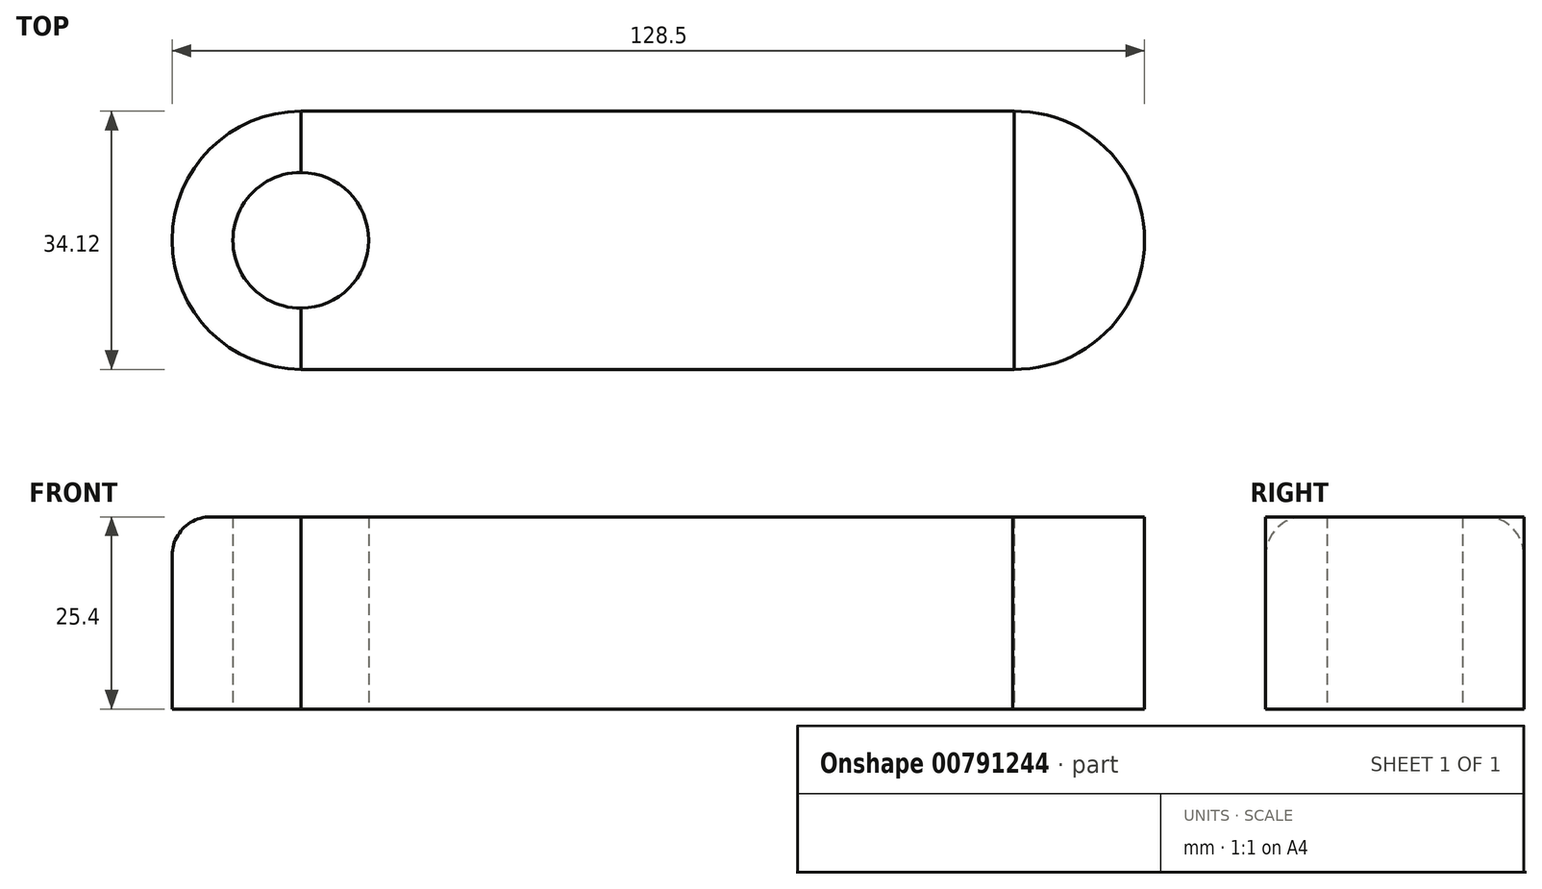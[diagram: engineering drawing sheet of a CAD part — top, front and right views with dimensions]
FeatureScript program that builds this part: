
annotation { "Feature Type Name" : "Feature", "Feature Type Description" : "" }
export const myFeature = defineFeature(function(context is Context, id is Id, definition is map)
    precondition{}
    {
        {
            var Q0;
            Q0=qCreatedBy(makeId("Top.planeOp"),FACE);
            var sketch = newSketch(context, id + "F0", { "sketchPlane" : qUnion([Q0])});
            skLineSegment(sketch, "E0.bottom", {"start": v(-47.1, 17.05) * mm, "end": v(47.1, 17.05) * mm});
            skLineSegment(sketch, "E0.top", {"start": v(-47.1, -17.05) * mm, "end": v(47.1, -17.05) * mm});
            skLineSegment(sketch, "E0.left", {"start": v(-47.1, 17.05) * mm, "end": v(-47.1, -17.05) * mm});
            skLineSegment(sketch, "E0.right", {"start": v(47.1, 17.05) * mm, "end": v(47.1, -17.05) * mm});
            skPoint(sketch, "E0.middle", {"position": v(0, 0) * mm});
            skSolve(sketch);
        }
        {
            var Q0;
            Q0=makeQuery(id+"F0.imprint","IMPRINT",FACE,{"disambiguationData":[TD([[makeQuery(id+"F0.imprint","IMPRINT",EDGE,{"derivedFrom":sQuery(id+"F0.wireOp",EDGE,"E0.bottom")}),-1.0]])]});
            var sketch = newSketch(context, id + "F1", { "sketchPlane" : qUnion([Q0])});
            skCircle(sketch, "E1", {"center": v(-47.1, 0) * mm, "radius": 17.05 * mm});
            skCircle(sketch, "E2", {"center": v(47.29, 0) * mm, "radius": 17.06 * mm});
            skSolve(sketch);
        }
        {
            var Q0;
            Q0=makeQuery(id+"F0.imprint","IMPRINT",FACE,{"disambiguationData":[TD([[makeQuery(id+"F0.imprint","IMPRINT",EDGE,{"derivedFrom":sQuery(id+"F0.wireOp",EDGE,"E0.bottom")}),-1.0]])]});
            var Q1;
            {var subQ5=makeQuery(id+"F0.imprint","IMPRINT",EDGE,{"derivedFrom":sQuery(id+"F0.wireOp",EDGE,"E0.right")});Q1=makeQuery(id+"F1.imprint","IMPRINT",FACE,{"disambiguationData":[TD([[makeQuery(id+"F1.imprint","IMPRINT",EDGE,{"derivedFrom":subQ5}),1.0]])]});}
            var Q2;
            {var subQ1=makeQuery(id+"F0.imprint","IMPRINT",EDGE,{"derivedFrom":sQuery(id+"F0.wireOp",EDGE,"E0.left")});Q2=makeQuery(id+"F1.imprint","IMPRINT",FACE,{"disambiguationData":[TD([[makeQuery(id+"F1.imprint","IMPRINT",EDGE,{"derivedFrom":subQ1}),-1.0]])]});}
            extrude(context, id + "F2", {"entities" : qUnion([Q0, Q1, Q2]), "depth" : 25.4 * mm, "offsetDistance" : 25.4 * mm});
        }
        {
            var Q0;
            Q0=qCreatedBy(makeId("Top.planeOp"),FACE);
            var sketch = newSketch(context, id + "F3", { "sketchPlane" : qUnion([Q0])});
            skCircle(sketch, "E3", {"center": v(-47.16, 0) * mm, "radius": 8.96 * mm});
            skCircle(sketch, "E4", {"center": v(47, 0) * mm, "radius": 9.34 * mm});
            skSolve(sketch);
        }
        {
            var Q0;
            Q0=makeQuery(id+"F3.imprint","IMPRINT",FACE,{"disambiguationData":[TD([[makeQuery(id+"F3.imprint","IMPRINT",EDGE,{"derivedFrom":sQuery(id+"F3.wireOp",EDGE,"E3")}),1.0]])]});
            extrude(context, id + "F4", {"entities" : qUnion([Q0]), "operationType" : NewBodyOperationType.REMOVE, "depth" : 40.64 * mm, "offsetDistance" : 25.4 * mm});
        }
        {
            var Q0;
            Q0=makeQuery(id+"F2.opExtrude","CAP_EDGE",EDGE,{"disambiguationData":[OSD([sQuery(id+"F1.wireOp",EDGE,"E1")])],"isStart":false});
            var Q1;
            Q1=makeQuery(id+"F2.opExtrude","SWEPT_FACE",FACE,{"disambiguationData":[OSD([sQuery(id+"F1.wireOp",EDGE,"E2")])]});
            fillet(context, id + "F5", {"entities" : qUnion([Q0, Q1]), "radius" : 5.08 * mm, "tangentPropagation" : true, "allowEdgeOverflow" : false});
        }
    });
